# Revit family: ALCR1277
name_source: partatom
category: Communication Devices
revit_build: Autodesk Revit 2014 (Build: 20130308_1515(x64)
units: mm (PartAtom-declared; Revit-internal decimal feet)

## types (1)
- ALCR1277
    Assembly Code = D5090
    Certification = UL and cUL Listed
    Default Elevation = 48 "
    Description = UL924, Emergency load control relay, with 0-10 V dimming override, 120-277VAC
    Features = Meets NEC Article 700 requirements for emergency lighting
• Dual voltage, 120 or 277V operation
• Normally closed contacts for emergency lighting
• Normally open contacts for 0–10V dimming override
• Provision for remote test button or fire alarm interface
• Multi-color function LED
• Suitable for use in return air plenums
• 5 year warranty
    Housing Material = Paint - Hubbell - Carbon Black
    L = 5.3 "
    Manufacturer = Hubbell Control Solutions
    Model = ALCR1277
    Type Comments = Power Packs and Relays
    URL = https://www.hubbell.com
    Warranty = 5-Years Warranty
    Washer = Metal-Hubbell-Galvanized_Steel

## geometry (parser evidence)
native form markers: Sweep x1
no freeform markers — native parametric forms only
